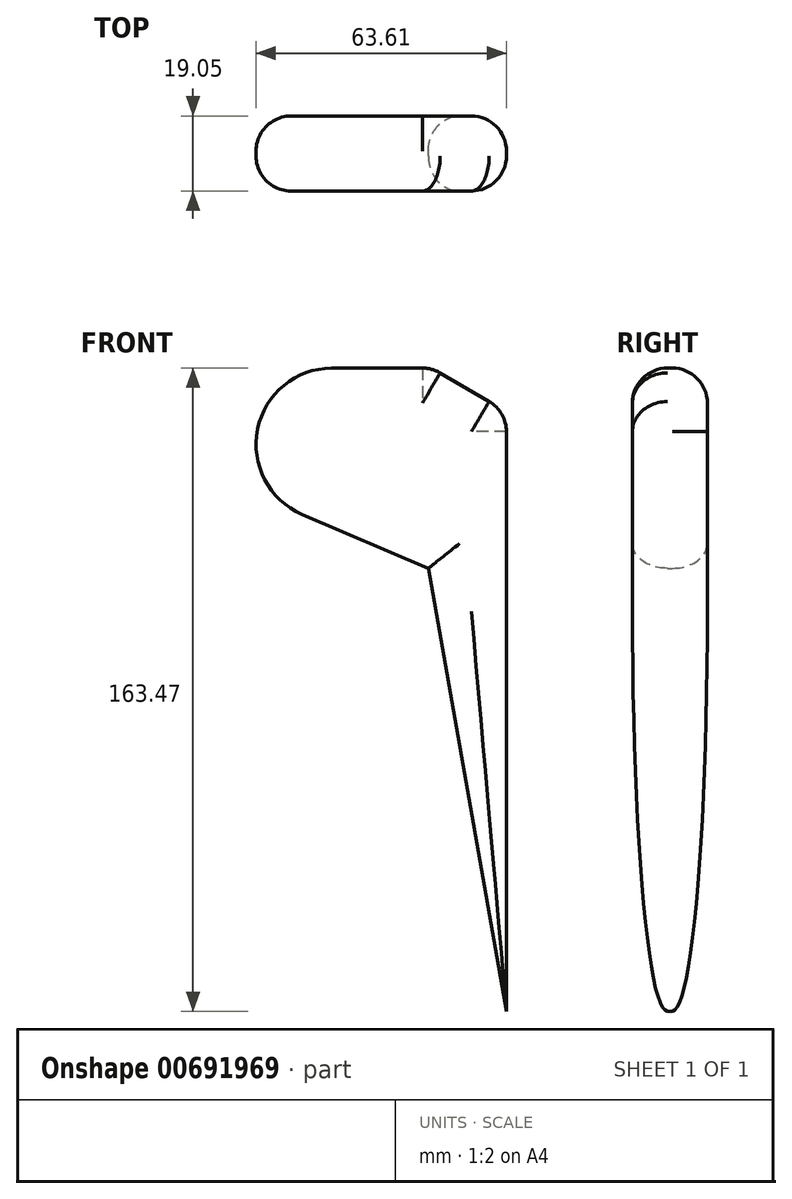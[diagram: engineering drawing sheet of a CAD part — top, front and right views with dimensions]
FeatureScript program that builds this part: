
annotation { "Feature Type Name" : "Feature", "Feature Type Description" : "" }
export const myFeature = defineFeature(function(context is Context, id is Id, definition is map)
    precondition{}
    {
        {
            var Q0;
            Q0=qCreatedBy(makeId("Front.planeOp"),FACE);
            var sketch = newSketch(context, id + "F0", { "sketchPlane" : qUnion([Q0])});
            skLineSegment(sketch, "E0", {"start": v(0, -112.6) * mm, "end": v(0, 39.8) * mm});
            skLineSegment(sketch, "E1", {"start": v(-18.92, 50.87) * mm, "end": v(-44.32, 50.87) * mm});
            skArc(sketch, "E2", {"start": v(-44.32, 50.87) * mm, "mid": v(-44.35, 50.87) * mm, "end": v(-44.38, 50.87) * mm});
            skArc(sketch, "E3", {"start": v(-44.38, 50.87) * mm, "mid": v(-63.23, 35.35) * mm, "end": v(-51.9, 13.74) * mm});
            skLineSegment(sketch, "E4", {"start": v(-51.9, 13.74) * mm, "end": v(-19.85, 0) * mm});
            skLineSegment(sketch, "E5", {"start": v(-19.85, 0) * mm, "end": v(0, -112.6) * mm});
            skLineSegment(sketch, "E6", {"start": v(-18.92, 50.87) * mm, "end": v(0, 39.8) * mm});
            skSolve(sketch);
        }
        {
            var Q0;
            Q0=makeQuery(id+"F0.imprint","IMPRINT",FACE,{"disambiguationData":[TD([[makeQuery(id+"F0.imprint","IMPRINT",EDGE,{"derivedFrom":sQuery(id+"F0.wireOp",EDGE,"E0")}),1.0]])]});
            extrude(context, id + "F1", {"entities" : qUnion([Q0]), "depth" : 19.05 * mm, "offsetDistance" : 25.4 * mm});
        }
        {
            var Q0;
            Q0=makeQuery(id+"F1.opExtrude","CAP_EDGE",EDGE,{"disambiguationData":[OSD([sQuery(id+"F0.wireOp",EDGE,"E3")])],"isStart":false});
            var Q1;
            Q1=makeQuery(id+"F1.opExtrude","CAP_EDGE",EDGE,{"disambiguationData":[OSD([sQuery(id+"F0.wireOp",EDGE,"E3")])],"isStart":true});
            var Q2;
            Q2=makeQuery(id+"F1.opExtrude","CAP_EDGE",EDGE,{"disambiguationData":[OSD([sQuery(id+"F0.wireOp",EDGE,"E4")])],"isStart":true});
            var Q3;
            Q3=makeQuery(id+"F1.opExtrude","CAP_EDGE",EDGE,{"disambiguationData":[OSD([sQuery(id+"F0.wireOp",EDGE,"E5")])],"isStart":false});
            var Q4;
            Q4=makeQuery(id+"F1.opExtrude","CAP_EDGE",EDGE,{"disambiguationData":[OSD([sQuery(id+"F0.wireOp",EDGE,"E5")])],"isStart":true});
            var Q5;
            Q5=makeQuery(id+"F1.opExtrude","CAP_EDGE",EDGE,{"disambiguationData":[OSD([sQuery(id+"F0.wireOp",EDGE,"E4")])],"isStart":false});
            var Q6;
            Q6=makeQuery(id+"F1.opExtrude","CAP_EDGE",EDGE,{"disambiguationData":[OSD([sQuery(id+"F0.wireOp",EDGE,"E1")])],"isStart":false});
            var Q7;
            Q7=makeQuery(id+"F1.opExtrude","CAP_EDGE",EDGE,{"disambiguationData":[OSD([sQuery(id+"F0.wireOp",EDGE,"E0")])],"isStart":false});
            var Q8;
            Q8=makeQuery(id+"F1.opExtrude","CAP_EDGE",EDGE,{"disambiguationData":[OSD([sQuery(id+"F0.wireOp",EDGE,"E6")])],"isStart":false});
            var Q9;
            Q9=makeQuery(id+"F1.opExtrude","CAP_EDGE",EDGE,{"disambiguationData":[OSD([sQuery(id+"F0.wireOp",EDGE,"E0")])],"isStart":true});
            fillet(context, id + "F2", {"entities" : qUnion([Q0, Q1, Q2, Q3, Q4, Q5, Q6, Q7, Q8, Q9]), "radius" : 8.9 * mm, "tangentPropagation" : true, "allowEdgeOverflow" : false});
        }
        {
            var Q0;
            Q0=makeQuery(id+"F2.opFillet","BLEND_EDGE",EDGE,{"blendedFrom":[makeQuery(id+"F1.opExtrude","CAP_EDGE",EDGE,{"disambiguationData":[OSD([sQuery(id+"F0.wireOp",EDGE,"E1")])],"isStart":true}),makeQuery(id+"F1.opExtrude","SWEPT_FACE",FACE,{"disambiguationData":[OSD([sQuery(id+"F0.wireOp",EDGE,"E6")])]})],"blendedInto":[makeQuery(id+"F1.opExtrude","SWEPT_FACE",FACE,{"disambiguationData":[OSD([sQuery(id+"F0.wireOp",EDGE,"E6")])]})]});
            var Q1;
            Q1=makeQuery(id+"F2.opFillet","BLEND_EDGE",EDGE,{"blendedFrom":[makeQuery(id+"F1.opExtrude","CAP_EDGE",EDGE,{"disambiguationData":[OSD([sQuery(id+"F0.wireOp",EDGE,"E0")])],"isStart":true}),makeQuery(id+"F1.opExtrude","SWEPT_FACE",FACE,{"disambiguationData":[OSD([sQuery(id+"F0.wireOp",EDGE,"E6")])]})],"blendedInto":[makeQuery(id+"F1.opExtrude","SWEPT_FACE",FACE,{"disambiguationData":[OSD([sQuery(id+"F0.wireOp",EDGE,"E6")])]})]});
            fillet(context, id + "F3", {"entities" : qUnion([Q0, Q1]), "radius" : 8.9 * mm, "tangentPropagation" : true, "allowEdgeOverflow" : false});
        }
    });
